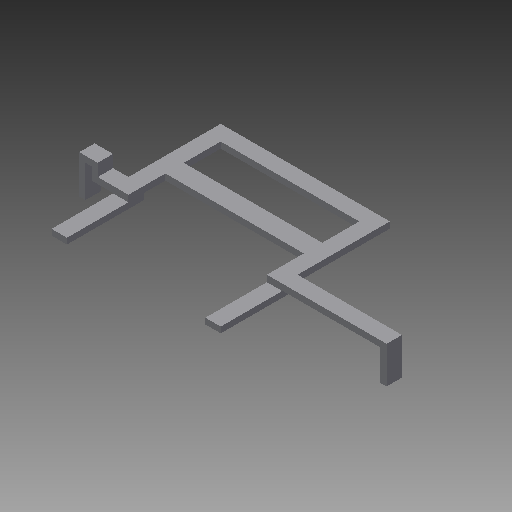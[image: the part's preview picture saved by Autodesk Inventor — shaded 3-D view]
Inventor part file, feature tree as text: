
AUTODESK INVENTOR PART (.ipt)
format: ipt  version: 2018.3 (Build 223284000, 284)  size: 208,384 bytes
history: native  units: mm
features: extrude x12, sketch x12
ambient origin geometry x8: Origin, YZ Plane, XZ Plane, XY Plane, X Axis, Y Axis, Z Axis, Center Point
bodies: Solid1 (feature_tree)
feature tree (24):
  extrude  "Extrusion1"  Depth=12.5mm
  extrude  "Extrusion2"  Depth=2.0mm
  extrude  "Extrusion3"  Depth=4.0mm
  extrude  "Extrusion4"  Depth=2.0mm
  extrude  "Extrusion5"  Depth=30.0mm TaperAngle=0.0deg
  extrude  "Extrusion6"  Depth=50.0mm TaperAngle=0.0deg
  extrude  "Extrusion7"  Depth=30.0mm TaperAngle=0.0deg
  extrude  "Extrusion8"  Depth=4.0mm TaperAngle=0.0deg
  extrude  "Extrusion9"  Depth=10.0mm TaperAngle=0.0deg
  extrude  "Extrusion10"  Depth=1.9mm
  extrude  "Extrusion11"  Depth=1.9mm
  extrude  "Extrusion12"  Depth=6.0mm
  sketch  "Sketch1"  dims[d0=2.0mm d1=12.5mm]
  sketch  "Sketch2"  dims[d2=4.0mm d3=2.0mm]
  sketch  "Sketch3"  dims[d4=2.0mm d5=4.0mm]
  sketch  "Sketch4"  dims[d6=5.0mm d7=0.0mm d8=2.0mm]
  sketch  "Sketch5"  dims[d9=10.0mm d10=0.0mm d11=30.0mm d12=0.0mm]
  sketch  "Sketch6"  dims[d13=5.0mm d14=50.0mm d15=0.0mm]
  sketch  "Sketch7"  dims[d16=5.0mm d17=30.0mm d18=0.0mm]
  sketch  "Sketch8"  dims[d19=29.93mm d20=0.0mm d21=4.0mm d22=0.0mm]
  sketch  "Sketch9"  dims[d23=2.0mm d24=10.0mm d25=0.0mm]
  sketch  "Sketch10"  dims[d26=2.0mm d27=0.0mm d28=1.9mm]
  sketch  "Sketch11"  dims[d29=20.0mm d30=0.0mm d31=1.9mm]
  sketch  "Sketch12"  dims[d32=20.0mm d33=0.0mm d34=6.0mm d35=12.0mm d36=10.0mm d37=0.0mm]
